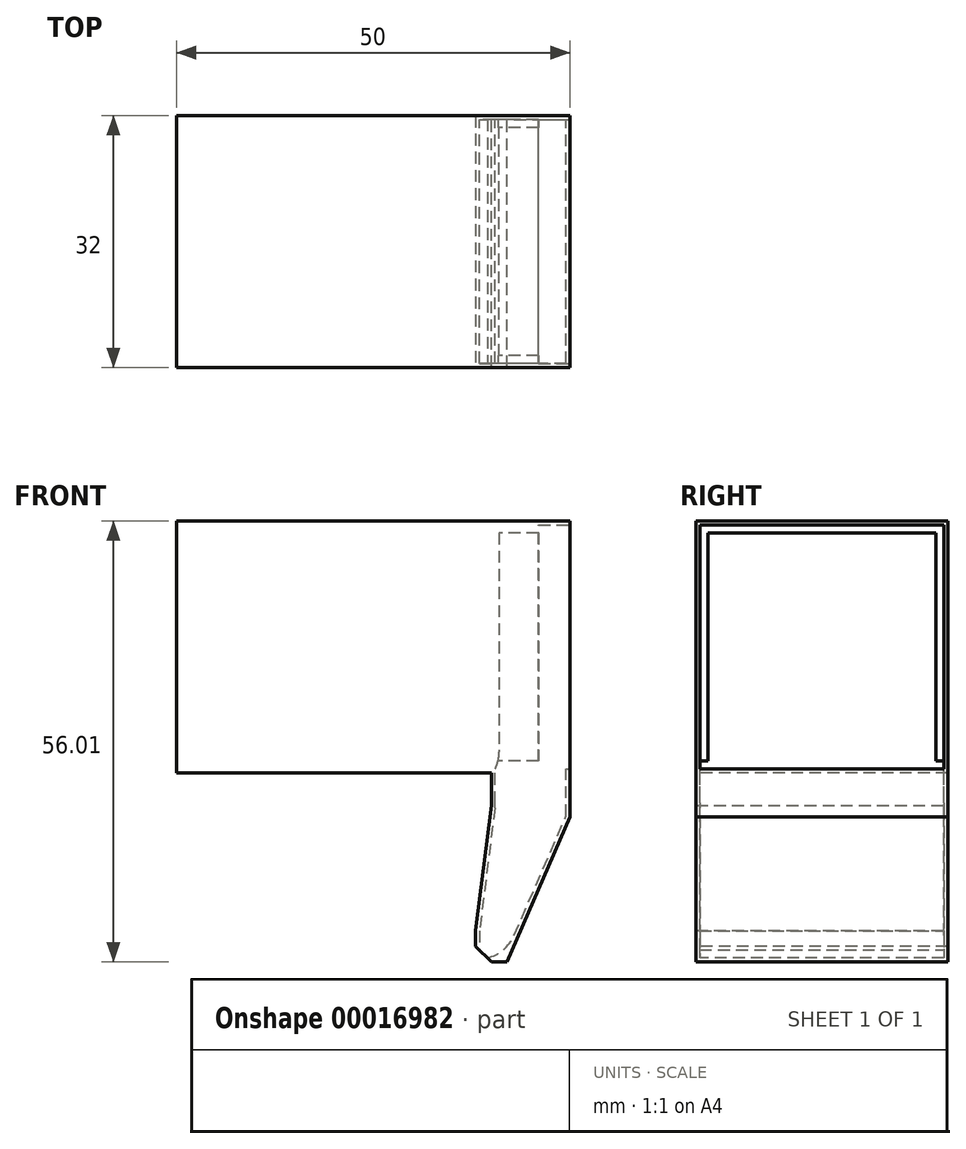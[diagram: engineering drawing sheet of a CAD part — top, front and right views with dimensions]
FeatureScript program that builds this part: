
annotation { "Feature Type Name" : "Feature", "Feature Type Description" : "" }
export const myFeature = defineFeature(function(context is Context, id is Id, definition is map)
    precondition{}
    {
        {
            var Q0;
            Q0=qCreatedBy(makeId("Right.planeOp"),FACE);
            var sketch = newSketch(context, id + "F0", { "sketchPlane" : qUnion([Q0])});
            skLineSegment(sketch, "E0.rect.bottom", {"start": v(16, -16) * mm, "end": v(-16, -16) * mm});
            skLineSegment(sketch, "E0.rect.top", {"start": v(16, 16) * mm, "end": v(-16, 16) * mm});
            skLineSegment(sketch, "E0.rect.left", {"start": v(16, -16) * mm, "end": v(16, 16) * mm});
            skLineSegment(sketch, "E0.rect.right", {"start": v(-16, -16) * mm, "end": v(-16, 16) * mm});
            skPoint(sketch, "E0.rect.middle", {"position": v(0, 0) * mm});
            skSolve(sketch);
        }
        {
            var Q0;
            Q0=makeQuery(id+"F0.imprint","IMPRINT",FACE,{"disambiguationData":[TD([[makeQuery(id+"F0.imprint","IMPRINT",EDGE,{"derivedFrom":sQuery(id+"F0.wireOp",EDGE,"E0.rect.bottom")}),-1.0]])]});
            extrude(context, id + "F1", {"entities" : qUnion([Q0]), "oppositeDirection" : true, "depth" : 40 * mm});
        }
        {
            var Q0;
            Q0=makeQuery(id+"F1.opExtrude","CAP_FACE",FACE,{"disambiguationData":[OSD([sQuery(id+"F0.wireOp",EDGE,"E0.rect.bottom"),sQuery(id+"F0.wireOp",EDGE,"E0.rect.top"),sQuery(id+"F0.wireOp",EDGE,"E0.rect.left"),sQuery(id+"F0.wireOp",EDGE,"E0.rect.right")])],"isStart":true});
            extrude(context, id + "F2", {"entities" : qUnion([Q0]), "depth" : 10 * mm});
        }
        {
            var Q0;
            {var subQ0=sQuery(id+"F0.wireOp",EDGE,"E0.rect.left");Q0=makeQuery(id+"F2.boolean.opBoolean","MERGE",FACE,{"derivedFrom":[makeQuery(id+"F1.opExtrude","SWEPT_FACE",FACE,{"disambiguationData":[OSD([subQ0])]}),makeQuery(id+"F2.opExtrude","SWEPT_FACE",FACE,{"disambiguationData":[OSD([subQ0])]})]});}
            var sketch = newSketch(context, id + "F3", { "sketchPlane" : qUnion([Q0])});
            skLineSegment(sketch, "E1", {"start": v(0, -16) * mm, "end": v(0, -20.1) * mm});
            skLineSegment(sketch, "E2", {"start": v(0, -20.1) * mm, "end": v(2, -36) * mm});
            skLineSegment(sketch, "E3", {"start": v(2, -36) * mm, "end": v(2, -40) * mm});
            skLineSegment(sketch, "E4", {"start": v(2, -40) * mm, "end": v(-2, -40) * mm});
            skLineSegment(sketch, "E5", {"start": v(-2, -40) * mm, "end": v(-10, -21.6) * mm});
            skLineSegment(sketch, "E6", {"start": v(-10, -21.6) * mm, "end": v(-10, -16) * mm});
            skLineSegment(sketch, "E7", {"start": v(-10, -16) * mm, "end": v(0, -16) * mm});
            skSolve(sketch);
        }
        {
            var Q0;
            Q0=makeQuery(id+"F3.imprint","IMPRINT",FACE,{"disambiguationData":[TD([[makeQuery(id+"F3.imprint","IMPRINT",EDGE,{"derivedFrom":sQuery(id+"F3.wireOp",EDGE,"E1")}),-1.0]])]});
            var Q1;
            {var subQ0=sQuery(id+"F0.wireOp",EDGE,"E0.rect.right");Q1=makeQuery(id+"F2.boolean.opBoolean","MERGE",FACE,{"derivedFrom":[makeQuery(id+"F1.opExtrude","SWEPT_FACE",FACE,{"disambiguationData":[OSD([subQ0])]}),makeQuery(id+"F2.opExtrude","SWEPT_FACE",FACE,{"disambiguationData":[OSD([subQ0])]})]});}
            extrude(context, id + "F4", {"entities" : qUnion([Q0]), "operationType" : NewBodyOperationType.ADD, "endBound" : BoundingType.UP_TO_SURFACE, "oppositeDirection" : true, "endBoundEntityFace" : qUnion([Q1]), "depth" : 25 * mm});
        }
        {
            var Q0;
            Q0=makeQuery(id+"F4.boolean.opBoolean","MERGE",FACE,{"derivedFrom":[makeQuery(id+"F2.opExtrude","CAP_FACE",FACE,{"disambiguationData":[OSD([sQuery(id+"F0.wireOp",EDGE,"E0.rect.bottom"),sQuery(id+"F0.wireOp",EDGE,"E0.rect.top"),sQuery(id+"F0.wireOp",EDGE,"E0.rect.left"),sQuery(id+"F0.wireOp",EDGE,"E0.rect.right")])],"isStart":false}),makeQuery(id+"F4.opExtrude","SWEPT_FACE",FACE,{"disambiguationData":[OSD([sQuery(id+"F3.wireOp",EDGE,"E6")])]})]});
            var sketch = newSketch(context, id + "F5", { "sketchPlane" : qUnion([Q0])});
            skLineSegment(sketch, "E8.rect.bottom", {"start": v(-15.5, -15.5) * mm, "end": v(15.5, -15.5) * mm});
            skLineSegment(sketch, "E8.rect.top", {"start": v(-15.5, 15.5) * mm, "end": v(15.5, 15.5) * mm});
            skLineSegment(sketch, "E8.rect.left", {"start": v(-15.5, -15.5) * mm, "end": v(-15.5, 15.5) * mm});
            skLineSegment(sketch, "E8.rect.right", {"start": v(15.5, -15.5) * mm, "end": v(15.5, 15.5) * mm});
            skPoint(sketch, "E8.rect.middle", {"position": v(0, 0) * mm});
            skSolve(sketch);
        }
        {
            var Q0;
            Q0=makeQuery(id+"F5.imprint","IMPRINT",FACE,{"disambiguationData":[TD([[makeQuery(id+"F5.imprint","IMPRINT",EDGE,{"derivedFrom":sQuery(id+"F5.wireOp",EDGE,"E8.rect.top")}),-1.0]])]});
            extrude(context, id + "F6", {"entities" : qUnion([Q0]), "operationType" : NewBodyOperationType.REMOVE, "oppositeDirection" : true, "depth" : 9 * mm});
        }
        {
            var Q0;
            Q0=makeQuery(id+"F4.opExtrude","SWEPT_EDGE",EDGE,{"disambiguationData":[OSD([sQuery(id+"F3.wireOp",EDGE,"E3"),sQuery(id+"F3.wireOp",EDGE,"E4")])]});
            chamfer(context, id + "F7", {"entities" : qUnion([Q0]), "width" : 2 * mm, "tangentPropagation" : true});
        }
        {
            var Q0;
            Q0=makeQuery(id+"F6.boolean.opBoolean","COPY",FACE,{"derivedFrom":makeQuery(id+"F6.opExtrude","SWEPT_FACE",FACE,{"disambiguationData":[OSD([sQuery(id+"F5.wireOp",EDGE,"E8.rect.bottom")])]})});
            var Q1;
            Q1=makeQuery(id+"F7.opChamfer","BLEND_FACE",FACE,{"disambiguationData":[OSD([sQuery(id+"F3.wireOp",EDGE,"E3"),sQuery(id+"F3.wireOp",EDGE,"E4")])]});
            shell(context, id + "F8", {"entities" : qUnion([Q0, Q1]), "thickness" : .5 * mm});
        }
        {
            var Q0;
            Q0=makeQuery(id+"F6.boolean.opBoolean","COPY",FACE,{"derivedFrom":makeQuery(id+"F6.opExtrude","CAP_FACE",FACE,{"disambiguationData":[OSD([sQuery(id+"F5.wireOp",EDGE,"E8.rect.bottom"),sQuery(id+"F5.wireOp",EDGE,"E8.rect.top"),sQuery(id+"F5.wireOp",EDGE,"E8.rect.left"),sQuery(id+"F5.wireOp",EDGE,"E8.rect.right")])],"isStart":false})});
            var sketch = newSketch(context, id + "F9", { "sketchPlane" : qUnion([Q0])});
            skLineSegment(sketch, "E9.rect.bottom", {"start": v(-14.5, 14.5) * mm, "end": v(14.5, 14.5) * mm});
            skLineSegment(sketch, "E9.rect.left", {"start": v(-14.5, 14.5) * mm, "end": v(-14.5, -14.5) * mm});
            skLineSegment(sketch, "E9.rect.right", {"start": v(14.5, 14.5) * mm, "end": v(14.5, -14.5) * mm});
            skPoint(sketch, "E9.rect.middle", {"position": v(0, 0) * mm});
            skLineSegment(sketch, "E10", {"start": v(-14.5, -14.5) * mm, "end": v(-15.5, -14.5) * mm});
            skLineSegment(sketch, "E11", {"start": v(-15.5, -14.5) * mm, "end": v(-15.5, 15.5) * mm});
            skLineSegment(sketch, "E12", {"start": v(-15.5, 15.5) * mm, "end": v(15.5, 15.5) * mm});
            skLineSegment(sketch, "E13", {"start": v(15.5, 15.5) * mm, "end": v(15.5, -14.5) * mm});
            skLineSegment(sketch, "E14", {"start": v(15.5, -14.5) * mm, "end": v(14.5, -14.5) * mm});
            skSolve(sketch);
        }
        {
            var Q0;
            Q0=makeQuery(id+"F9.imprint","IMPRINT",FACE,{"disambiguationData":[TD([[makeQuery(id+"F9.imprint","IMPRINT",EDGE,{"derivedFrom":sQuery(id+"F9.wireOp",EDGE,"E9.rect.bottom")}),1.0]])]});
            extrude(context, id + "F10", {"entities" : qUnion([Q0]), "operationType" : NewBodyOperationType.ADD, "depth" : 5 * mm});
        }
        {
            var Q0;
            Q0=makeQuery(id+"F6.boolean.opBoolean","COPY",EDGE,{"derivedFrom":makeQuery(id+"F6.opExtrude","CAP_EDGE",EDGE,{"disambiguationData":[OSD([sQuery(id+"F5.wireOp",EDGE,"E8.rect.bottom")])],"isStart":false})});
            var Q1;
            Q1=makeQuery(id+"F8.opShell","OFFSET_EDGE",EDGE,{"disambiguationData":[OSD([sQuery(id+"F3.wireOp",EDGE,"E1"),sQuery(id+"F3.wireOp",EDGE,"E2")])]});
            fillet(context, id + "F11", {"entities" : qUnion([Q0, Q1]), "radius" : 5 * mm, "tangentPropagation" : true, "allowEdgeOverflow" : false});
        }
        {
            var Q0;
            Q0=makeQuery(id+"F8.opShell","OFFSET_EDGE",EDGE,{"disambiguationData":[OSD([sQuery(id+"F3.wireOp",EDGE,"E4"),sQuery(id+"F3.wireOp",EDGE,"E5")])]});
            fillet(context, id + "F12", {"entities" : qUnion([Q0]), "radius" : 5 * mm, "tangentPropagation" : true, "allowEdgeOverflow" : false});
        }
    });
